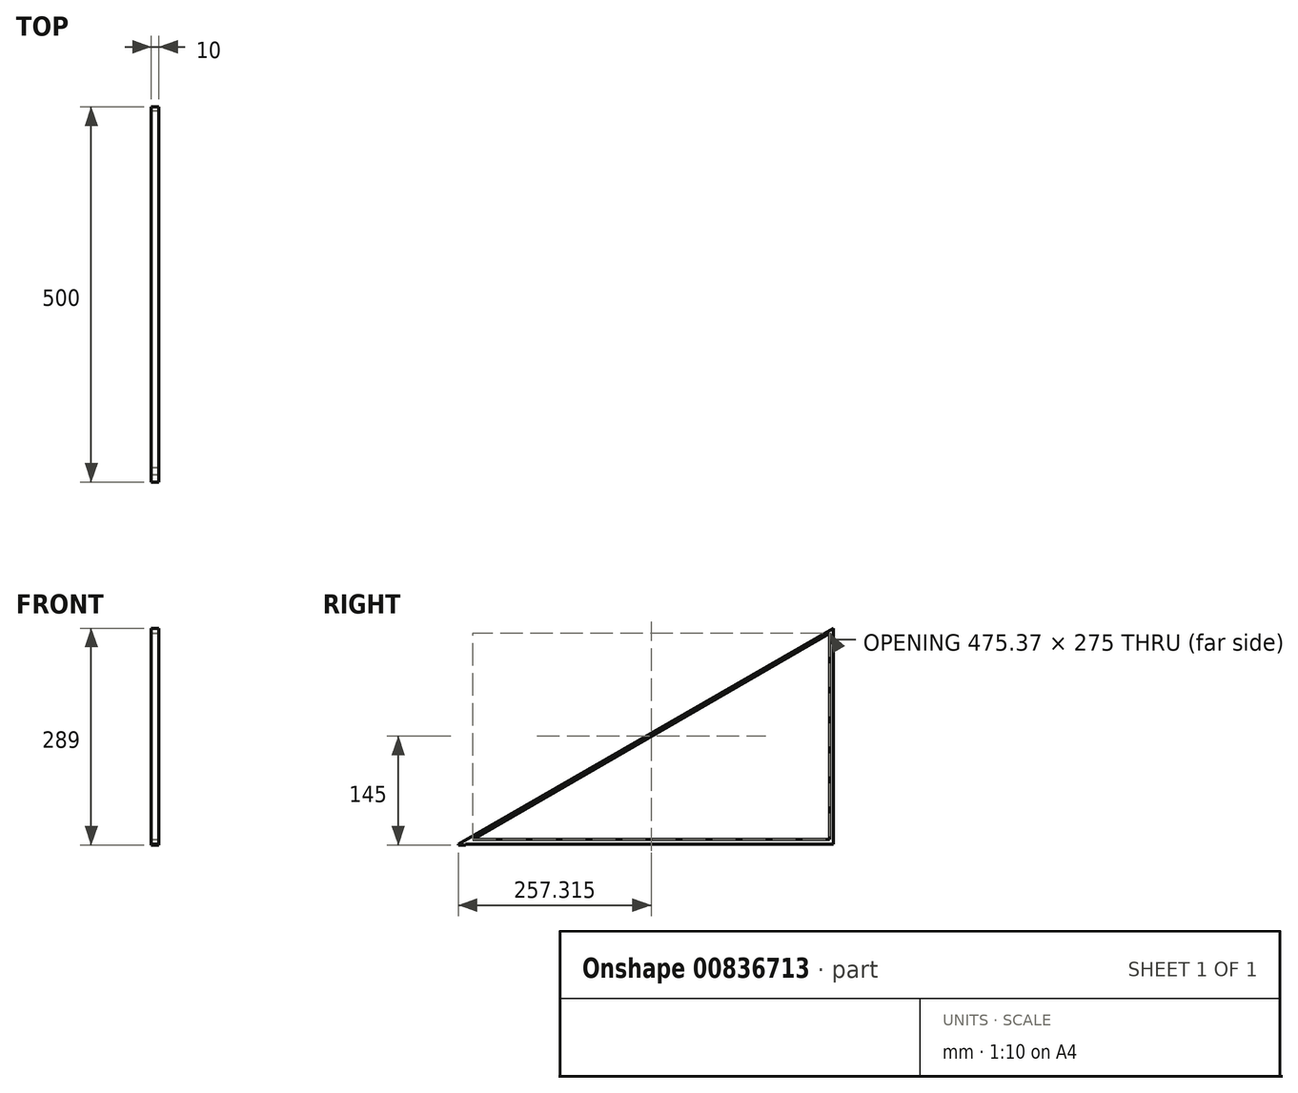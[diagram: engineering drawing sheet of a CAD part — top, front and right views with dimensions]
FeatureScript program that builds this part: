
annotation { "Feature Type Name" : "Feature", "Feature Type Description" : "" }
export const myFeature = defineFeature(function(context is Context, id is Id, definition is map)
    precondition{}
    {
        {
            var Q0;
            Q0=qCreatedBy(makeId("Top.planeOp"),FACE);
            var sketch = newSketch(context, id + "F0", { "sketchPlane" : qUnion([Q0])});
            skLineSegment(sketch, "E0", {"start": v(1.48, 497.37) * mm, "end": v(11.48, 497.37) * mm});
            skLineSegment(sketch, "E1", {"start": v(11.48, 497.37) * mm, "end": v(11.48, -2.63) * mm});
            skLineSegment(sketch, "E2", {"start": v(11.48, -2.63) * mm, "end": v(1.48, -2.63) * mm});
            skLineSegment(sketch, "E3", {"start": v(1.48, -2.63) * mm, "end": v(1.48, 497.37) * mm});
            skSolve(sketch);
        }
        {
            var Q0;
            Q0 = qSketchRegion(id + "F0", true);
            extrude(context, id + "F1", {"entities" : qUnion([Q0]), "depth" : 288 * mm, "offsetDistance" : 25 * mm});
        }
        {
            var Q0;
            Q0=makeQuery(id+"F1.opExtrude","SWEPT_FACE",FACE,{"disambiguationData":[OSD([sQuery(id+"F0.wireOp",EDGE,"E3")])]});
            var sketch = newSketch(context, id + "F2", { "sketchPlane" : qUnion([Q0])});
            skLineSegment(sketch, "E4", {"start": v(-497.37, 288) * mm, "end": v(2.63, 0) * mm});
            skSolve(sketch);
        }
        {
            var Q0;
            Q0=makeQuery(id+"F2.imprint","IMPRINT",FACE,{"disambiguationData":[TD([[makeQuery(id+"F2.imprint","IMPRINT",EDGE,{"derivedFrom":sQuery(id+"F2.wireOp",EDGE,"E4")}),1.0]])]});
            extrude(context, id + "F3", {"entities" : qUnion([Q0]), "operationType" : NewBodyOperationType.REMOVE, "oppositeDirection" : true, "depth" : 10 * mm, "offsetDistance" : 25 * mm});
        }
        {
            var Q0;
            Q0=makeQuery(id+"F1.opExtrude","SWEPT_FACE",FACE,{"disambiguationData":[OSD([sQuery(id+"F0.wireOp",EDGE,"E1")])]});
            var sketch = newSketch(context, id + "F4", { "sketchPlane" : qUnion([Q0])});
            skPoint(sketch, "E5", {"position": v(492.37, 6.5) * mm});
            skPoint(sketch, "E6", {"position": v(17, 6.5) * mm});
            skPoint(sketch, "E7", {"position": v(492.37, 281.5) * mm});
            skLineSegment(sketch, "E8", {"start": v(17, 6.5) * mm, "end": v(492.37, 6.5) * mm});
            skLineSegment(sketch, "E9", {"start": v(492.37, 6.5) * mm, "end": v(492.37, 281.5) * mm});
            skLineSegment(sketch, "E10", {"start": v(17, 6.5) * mm, "end": v(492.37, 281.5) * mm});
            skSolve(sketch);
        }
        {
            var Q0;
            Q0=makeQuery(id+"F4.imprint","IMPRINT",FACE,{"disambiguationData":[TD([[makeQuery(id+"F4.imprint","IMPRINT",EDGE,{"derivedFrom":sQuery(id+"F4.wireOp",EDGE,"E8")}),1.0]])]});
            extrude(context, id + "F5", {"entities" : qUnion([Q0]), "operationType" : NewBodyOperationType.REMOVE, "oppositeDirection" : true, "depth" : 10 * mm, "offsetDistance" : 25 * mm});
        }
        {
            var Q0;
            Q0=makeQuery(id+"F1.opExtrude","CAP_FACE",FACE,{"disambiguationData":[OSD([sQuery(id+"F0.wireOp",EDGE,"E0"),sQuery(id+"F0.wireOp",EDGE,"E1"),sQuery(id+"F0.wireOp",EDGE,"E2"),sQuery(id+"F0.wireOp",EDGE,"E3")])],"isStart":true});
            var sketch = newSketch(context, id + "F6", { "sketchPlane" : qUnion([Q0])});
            skLineSegment(sketch, "E11.bottom", {"start": v(1.48, 2.63) * mm, "end": v(11.48, 2.63) * mm});
            skLineSegment(sketch, "E11.top", {"start": v(1.48, -7.37) * mm, "end": v(11.48, -7.37) * mm});
            skLineSegment(sketch, "E11.left", {"start": v(1.48, 2.63) * mm, "end": v(1.48, -7.37) * mm});
            skLineSegment(sketch, "E11.right", {"start": v(11.48, 2.63) * mm, "end": v(11.48, -7.37) * mm});
            skSolve(sketch);
        }
        {
            var Q0;
            Q0=makeQuery(id+"F6.imprint","IMPRINT",FACE,{"disambiguationData":[TD([[makeQuery(id+"F6.imprint","IMPRINT",EDGE,{"derivedFrom":sQuery(id+"F6.wireOp",EDGE,"E11.bottom")}),1.0]])]});
            extrude(context, id + "F7", {"entities" : qUnion([Q0]), "operationType" : NewBodyOperationType.ADD, "depth" : 1 * mm, "offsetDistance" : 25 * mm});
        }
    });
